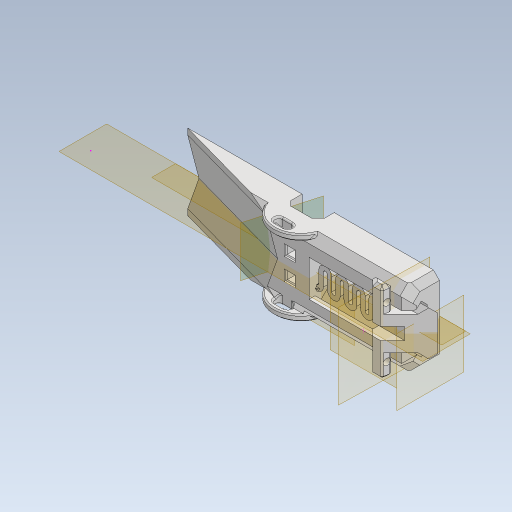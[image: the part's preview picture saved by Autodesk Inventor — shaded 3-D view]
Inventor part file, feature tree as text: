
AUTODESK INVENTOR PART (.ipt)
format: ipt  version: 2023 (Build 270158030, 158C)  size: 775,680 bytes
history: native  units: mm
features: extrude x16, sketch x15, chamfer x13, reference x8, plane x7, other x6, projected_geometry x6, fillet x5, mirror x2
ambient origin geometry x8: Origin, YZ Plane, XZ Plane, XY Plane, X Axis, Y Axis, Z Axis, Center Point
bodies: Body1 (feature_tree), Body2 (feature_tree)
feature tree (78):
  other  "ramp"
  extrude  "Extrusion1"  Depth=10.0mm
  extrude  "Extrusion2"  Depth=10.0mm
  chamfer  "Chamfer2"  Distance=25.0mm
  plane  "Work Plane3"
  extrude  "Extrusion4"  Depth=2.0mm TaperAngle=45.0deg
  chamfer  "Chamfer4"  Distance=1.5mm Angle=45.0deg
  plane  "Work Plane4"
  chamfer  "Chamfer15"  Distance=33.0mm
  sketch  "Sketch5"  dims[d11=33.0mm d12=0.0mm d21=2.0mm d22=2.0mm d23=45.0deg]
  extrude  "Extrusion18"  TaperAngle=90.0deg  [1 undecoded]
  chamfer  "Chamfer16"  [1 undecoded]
  extrude  "Extrusion19"  Depth=3.0mm
  fillet  "Fillet3"  [1 undecoded]
  fillet  "Fillet4"  Radius=2.0mm
  plane  "Work Plane5"
  extrude  "Extrusion20"  Depth=4.0mm
  fillet  "Fillet5"  Radius=4.0mm
  fillet  "Fillet6"  [1 undecoded]
  extrude  "Extrusion8"  Depth=2.0mm
  extrude  "Extrusion9"  Depth=2.0mm
  plane  "Work Plane1"
  extrude  "Extrusion10"  Depth=0.5mm
  extrude  "Extrusion11"  Depth=0.3mm
  extrude  "Extrusion21"  Depth=0.5mm
  chamfer  "Chamfer18"  Distance=5.5mm Angle=45.0deg
  extrude  "Extrusion12"  Depth=0.5mm
  plane  "Work Plane2"
  mirror  "Mirror1"
  chamfer  "Chamfer8"  Distance=4.0mm
  chamfer  "Chamfer19"  Distance=2.5mm
  extrude  "Extrusion22"  Depth=1.0mm TaperAngle=45.0deg
  chamfer  "Chamfer20"  Distance=2.5mm
  chamfer  "Chamfer21"  Distance=2.75mm
  chamfer  "Chamfer22"  Distance=2.75mm
  extrude  "Extrusion23"  Depth=0.5mm
  chamfer  "Chamfer23"  Distance=2.75mm
  chamfer  "Chamfer24"  Distance=2.75mm
  plane  "Work Plane6"
  extrude  "Extrusion24"  Depth=0.5mm
  chamfer  "Chamfer25"  Distance=2.75mm
  extrude  "Extrusion25"  Depth=0.5mm
  fillet  "Fillet7"  Radius=3.0mm
  plane  "Work Plane7"
  mirror  "Mirror2"
  reference  "Reference1"
  reference  "Reference2"
  reference  "Reference3"
  reference  "Reference4"
  reference  "Reference5"
  reference  "Reference6"
  sketch  "Sketch2"  dims[d0=10.0mm d1=35.0mm]
  projected_geometry  "Projected Loop1"
  sketch  "Sketch4"  dims[d2=15.0mm d3=10.0mm d4=25.0mm d5=0.0mm]
  projected_geometry  "Projected Loop3"
  sketch  "Sketch9"  dims[d27=4.0mm d28=10.0mm d29=0.0mm d30=0.0mm d34=1.5mm d35=2.0mm d36=45.0deg d74=33.0mm d75=0.0mm]
  sketch  "Sketch10"  dims[d77=0.0mm d78=0.0mm d79=90.0deg]
  sketch  "Sketch11"  dims[d80=1.0mm]
  sketch  "Sketch12"  dims[d81=10.5mm]
  projected_geometry  "Projected Loop4"
  other  "slide"
  reference  "Reference17"
  sketch  "Sketch20"  dims[d82=10.5mm d83=0.0mm d84=0.0mm]
  sketch  "Sketch21"  dims[d86=3.0mm d89=3.0mm d91=0.0mm d92=0.0mm d96=2.0mm d97=0.0mm]
  sketch  "Sketch23"  dims[d98=0.4mm d99=2.0mm d100=45.0deg d144=4.0mm d145=4.0mm d146=45.0deg]
  projected_geometry  "Projected Loop8"
  reference  "Reference18"
  sketch  "Sketch24"  dims[d147=45.0deg d149=2.0mm]
  projected_geometry  "Projected Loop9"
  sketch  "Sketch25"  dims[d150=2.0mm d151=2.0mm]
  sketch  "Sketch27"  dims[d152=0.5mm d153=0.3mm]
  projected_geometry  "Projected Loop10"
  sketch  "Sketch28"  dims[d154=0.3mm d155=0.3mm]
  sketch  "Sketch29"  dims[d156=0.3mm d157=0.5mm d158=5.5mm d159=2.0mm d160=45.0deg d161=4.0mm d162=4.0mm d163=2.5mm d164=0.0mm d165=1.0mm d166=2.0mm d167=45.0deg d176=2.5mm d177=2.75mm d178=2.75mm d179=2.75mm d180=2.75mm d181=2.75mm d182=2.75mm d184=1.5mm d185=2.75mm d186=2.75mm d187=3.0mm d188=2.0mm d189=1.5mm d190=1.25mm d191=1.25mm d192=3.0mm d193=0.0mm d194=0.625mm d195=2.125mm d196=1.0mm d197=2.0mm d198=0.75mm d199=0.1mm d200=2.4mm d201=0.0mm d205=1.0mm d206=1.0mm d207=1.8mm d208=0.3mm d209=0.3mm d210=0.5mm d211=0.0mm d212=0.3mm d213=2.0mm d214=45.0deg d215=9.0mm d217=5.0mm d218=1.0mm d219=2.0mm d220=45.0deg d221=3.5mm d222=3.5mm d223=4.0mm d224=0.0mm d225=4.0mm d226=2.0mm d227=45.0deg d228=2.0mm d229=2.0mm d230=45.0deg d231=2.5mm d232=2.0mm d233=45.0deg d238=0.5mm d239=7.75mm d240=0.0mm d241=2.5mm d242=2.0mm d243=45.0deg d244=1.0mm d245=2.0mm d246=45.0deg d247=2.1mm d248=3.0mm d249=1.0mm d250=-1.745329mm d251=0.0mm d252=0.0mm d253=1.0mm d254=2.0mm d255=45.0deg d256=2.5mm d257=3.0mm d258=6.5mm d259=0.0mm d260=0.0mm d261=0.5mm]
  other  "<userpath>\Documents\0004-inventor\3D-CAD-main\trebuchet\V4.0-trebuchet-assembled.iam"
  other  "V4.0-trebuchet-assembled.iam"
  other  "V4-baseplate:1"
  other  "V4-throw-arm:1"
note: 4 required parameter values undecoded (feature->parameter linkage not recoverable at this tier; creation-order binding heuristic only, values carry confidence <= 0.55)
